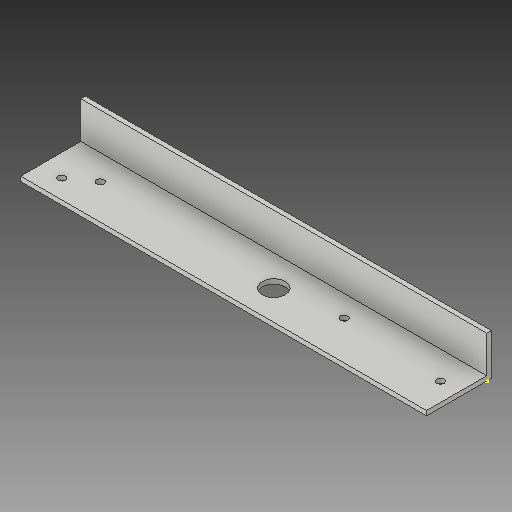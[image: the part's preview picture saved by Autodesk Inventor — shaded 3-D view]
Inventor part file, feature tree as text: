
AUTODESK INVENTOR PART (.ipt)
format: ipt  version: 2018 (Build 220112000, 112)  size: 138,240 bytes
history: native  units: in
note: dims shown in document units (in); Inventor stores cm internally (conversion verified against a paired STEP export)
features: other x8, sketch x7, reference x5, extrude x2
ambient origin geometry x8: Origin, YZ Plane, XZ Plane, XY Plane, X Axis, Y Axis, Z Axis, Center Point
bodies: Solid1 (feature_tree)
feature tree (22):
  other  "angle iron with  holes 2.ipt"
  extrude  "Extrusion1"  Depth=0.3937in
  sketch  "Sketch6"  dims[d8=0.2031in]
  extrude  "Extrusion2"  Depth=0.2031in
  other  "Solid1::angle iron with  holes 2.ipt"
  other  "TaggingFeature1"
  sketch  "Sketch1"  dims[d0=0.3937in d1=0.625in]
  sketch  "Sketch2"  dims[d2=0.2031in d3=0.2031in]
  sketch  "Sketch3"  dims[d4=1.0in d5=0.0in]
  sketch  "Sketch4"  dims[d6=1.0497in]
  sketch  "Sketch5"  dims[d7=3.3in]
  reference  "Reference1"
  reference  "Reference2"
  reference  "Reference3"
  sketch  "Sketch7"  dims[d9=1.0in d10=0.0in]
  reference  "Reference4"
  reference  "Reference5"
  other  "USE THIS main gripper assembly.iam"
  other  "motor assembly_MIR:1"
  other  "VersaPlanetary_v2_Single_Stage_10_1_with_775_Series_MIR:1"
  other  "eye screw stand-in:1"
  other  "base mount:1"
